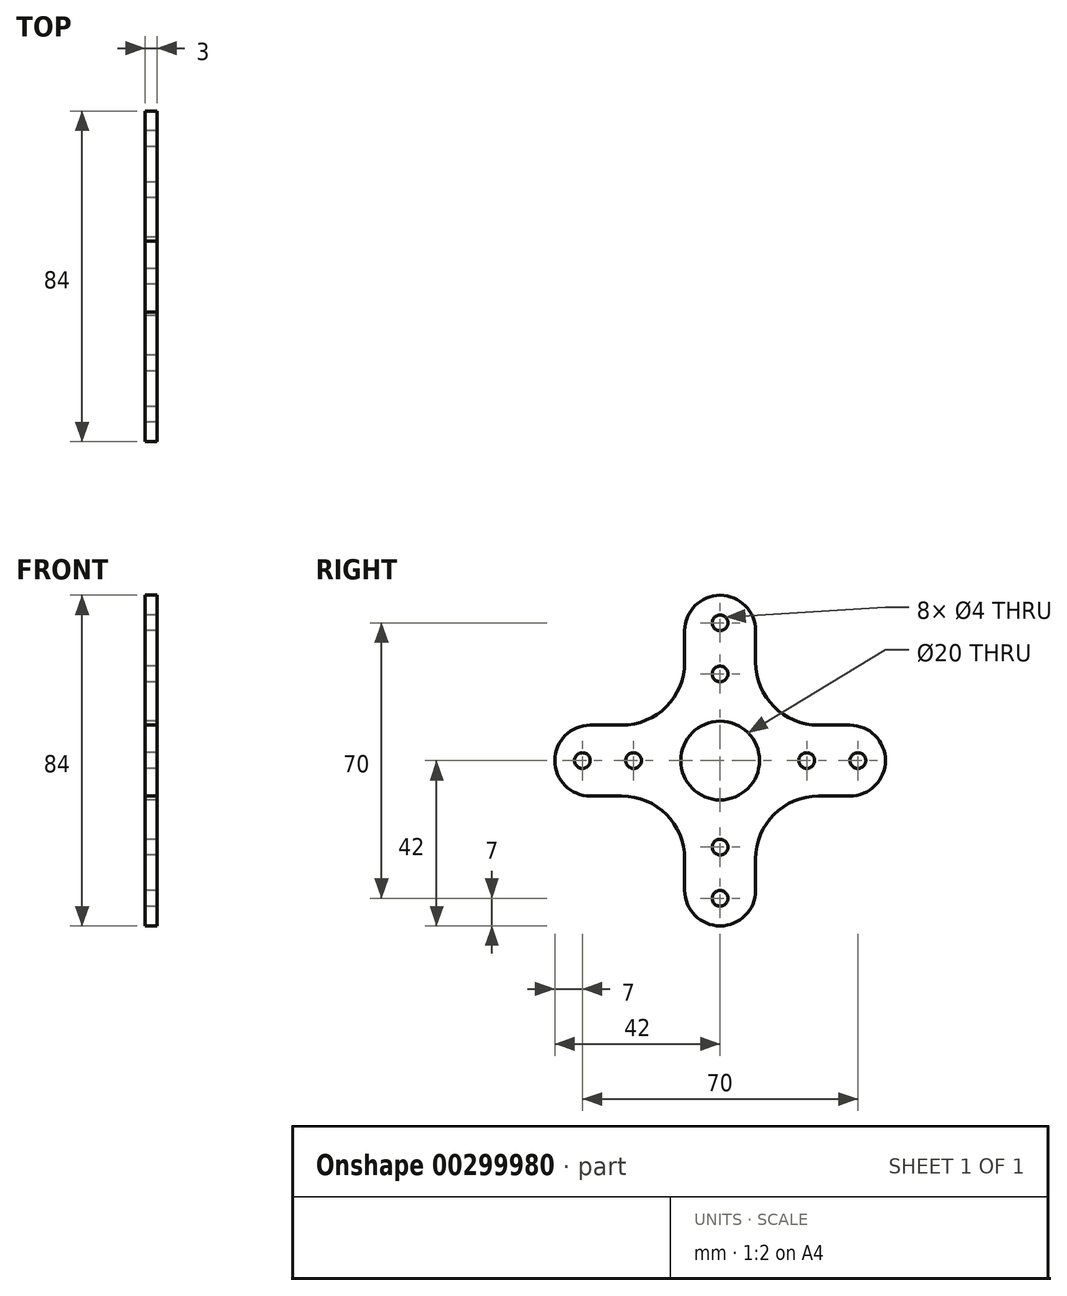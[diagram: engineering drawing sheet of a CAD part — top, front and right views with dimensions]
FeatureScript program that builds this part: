
annotation { "Feature Type Name" : "Feature", "Feature Type Description" : "" }
export const myFeature = defineFeature(function(context is Context, id is Id, definition is map)
    precondition{}
    {
        {
            var Q0;
            Q0=qCreatedBy(makeId("Right.planeOp"),FACE);
            var sketch = newSketch(context, id + "F0", { "sketchPlane" : qUnion([Q0])});
            skLineSegment(sketch, "E0", {"start": v(-42, 0) * mm, "end": v(42, 0) * mm});
            skLineSegment(sketch, "E1", {"start": v(0, 42) * mm, "end": v(0, -42) * mm});
            skCircle(sketch, "E2", {"center": v(0, 33) * mm, "radius": 9 * mm});
            skCircle(sketch, "E3", {"center": v(33, 0) * mm, "radius": 9 * mm});
            skCircle(sketch, "E4", {"center": v(0, -33) * mm, "radius": 9 * mm});
            skCircle(sketch, "E5", {"center": v(-33, 0) * mm, "radius": 9 * mm});
            skLineSegment(sketch, "E6", {"start": v(-33, 0) * mm, "end": v(-33, 9) * mm});
            skLineSegment(sketch, "E7", {"start": v(25, 9) * mm, "end": v(33, 9) * mm});
            skLineSegment(sketch, "E8", {"start": v(33, 0) * mm, "end": v(33, -9) * mm});
            skLineSegment(sketch, "E9", {"start": v(33, -9) * mm, "end": v(25, -9) * mm});
            skLineSegment(sketch, "E10", {"start": v(0, 33) * mm, "end": v(-9, 33) * mm});
            skLineSegment(sketch, "E11", {"start": v(-9, -25) * mm, "end": v(-9, -33) * mm});
            skLineSegment(sketch, "E12", {"start": v(-9, -33) * mm, "end": v(9, -33) * mm});
            skLineSegment(sketch, "E13", {"start": v(9, 25) * mm, "end": v(9, 33) * mm});
            skCircle(sketch, "E14", {"center": v(0, 0) * mm, "radius": 10 * mm});
            skArc(sketch, "E15.filletArc", {"start": v(9, 25) * mm, "mid": v(13.69, 13.69) * mm, "end": v(25, 9) * mm});
            skLineSegment(sketch, "E16", {"start": v(9, -33) * mm, "end": v(9, -25) * mm});
            skArc(sketch, "E17.filletArc", {"start": v(25, -9) * mm, "mid": v(13.69, -13.69) * mm, "end": v(9, -25) * mm});
            skLineSegment(sketch, "E18", {"start": v(-33, 0) * mm, "end": v(-33, -9) * mm});
            skLineSegment(sketch, "E19", {"start": v(-33, -9) * mm, "end": v(-25, -9) * mm});
            skArc(sketch, "E20.filletArc", {"start": v(-9, -25) * mm, "mid": v(-13.69, -13.69) * mm, "end": v(-25, -9) * mm});
            skLineSegment(sketch, "E21", {"start": v(-33, 9) * mm, "end": v(-25, 9) * mm});
            skLineSegment(sketch, "E22", {"start": v(-9, 33) * mm, "end": v(-9, 25) * mm});
            skArc(sketch, "E23.filletArc", {"start": v(-25, 9) * mm, "mid": v(-13.69, 13.69) * mm, "end": v(-9, 25) * mm});
            skCircle(sketch, "E24", {"center": v(-35, 0) * mm, "radius": 2 * mm});
            skCircle(sketch, "E25", {"center": v(-22, 0) * mm, "radius": 2 * mm});
            skCircle(sketch, "E26.1.0", {"center": v(0, -22) * mm, "radius": 2 * mm});
            skCircle(sketch, "E26.1.1", {"center": v(0, -35) * mm, "radius": 2 * mm});
            skCircle(sketch, "E26.2.0", {"center": v(22, 0) * mm, "radius": 2 * mm});
            skCircle(sketch, "E26.2.1", {"center": v(35, 0) * mm, "radius": 2 * mm});
            skCircle(sketch, "E26.3.0", {"center": v(0, 22) * mm, "radius": 2 * mm});
            skCircle(sketch, "E26.3.1", {"center": v(0, 35) * mm, "radius": 2 * mm});
            skSolve(sketch);
        }
        {
            var Q0;
            Q0 = qSketchRegion(id + "F0", true);
            extrude(context, id + "F1", {"entities" : qUnion([Q0]), "depth" : 3 * mm, "offsetDistance" : 25 * mm});
        }
    });
